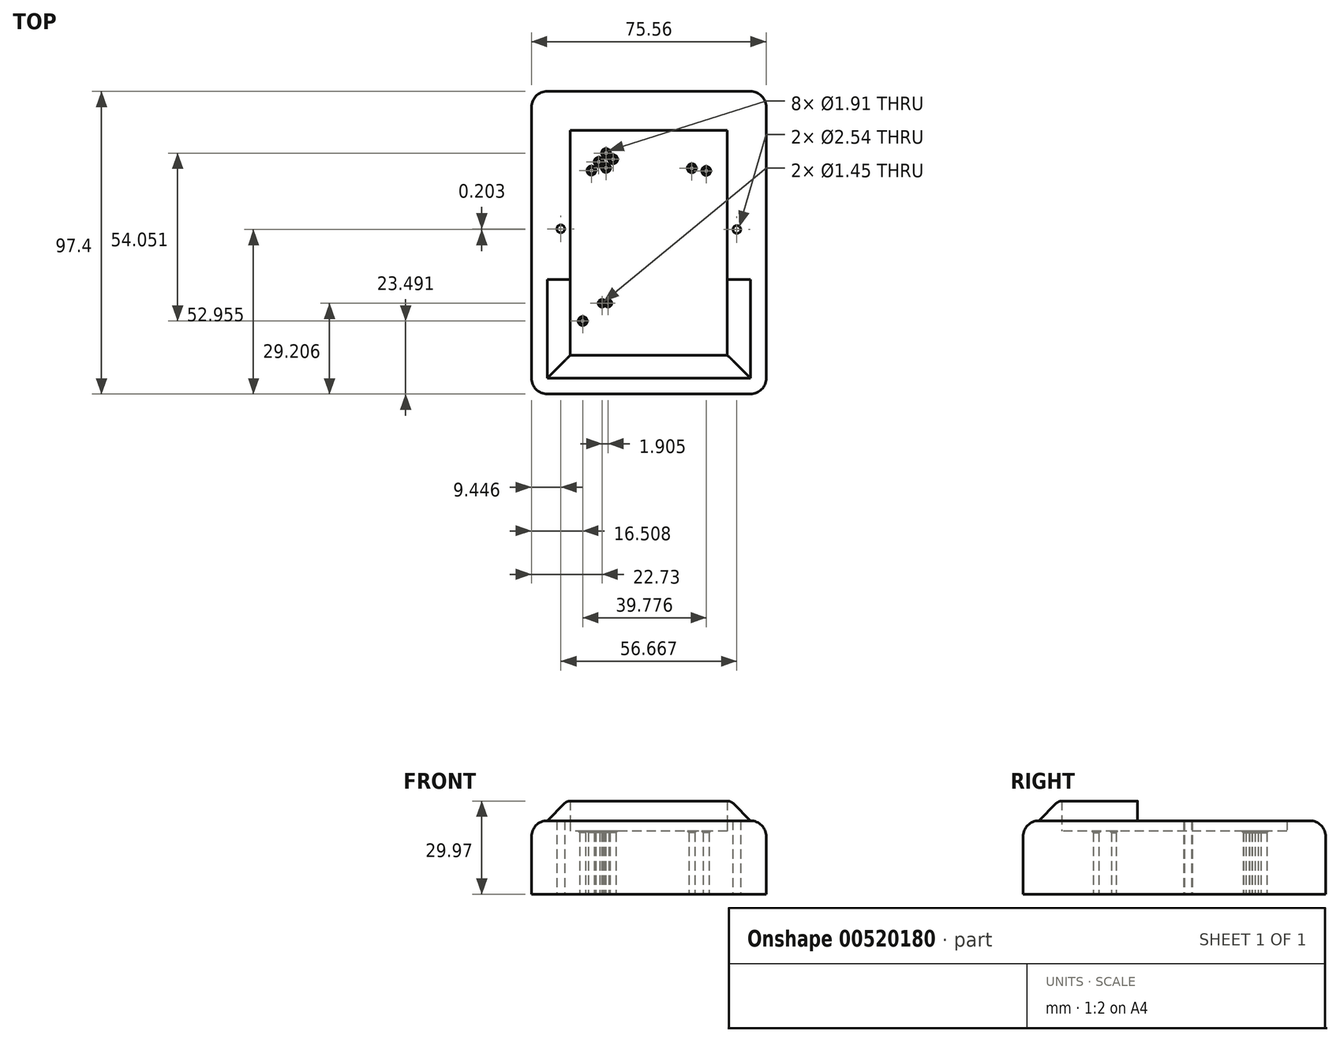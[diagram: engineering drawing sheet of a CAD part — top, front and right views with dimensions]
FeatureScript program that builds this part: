
annotation { "Feature Type Name" : "Feature", "Feature Type Description" : "" }
export const myFeature = defineFeature(function(context is Context, id is Id, definition is map)
    precondition{}
    {
        {
            var Q0;
            Q0=qCreatedBy(makeId("Top.planeOp"),FACE);
            var sketch = newSketch(context, id + "F0", { "sketchPlane" : qUnion([Q0])});
            skLineSegment(sketch, "E0.bottom", {"start": v(25.08, 36) * mm, "end": v(-25.08, 36) * mm});
            skLineSegment(sketch, "E0.top", {"start": v(25.08, -36) * mm, "end": v(-25.08, -36) * mm});
            skLineSegment(sketch, "E0.left", {"start": v(25.08, 36) * mm, "end": v(25.08, -36) * mm});
            skLineSegment(sketch, "E0.right", {"start": v(-25.08, 36) * mm, "end": v(-25.08, -36) * mm});
            skPoint(sketch, "E0.middle", {"position": v(0, 0) * mm});
            skCircle(sketch, "E1", {"center": v(-21.27, -25.2) * mm, "radius": 0.95 * mm});
            skCircle(sketch, "E2", {"center": v(-15.05, -19.5) * mm, "radius": 0.72 * mm});
            skCircle(sketch, "E3", {"center": v(-13.14, -19.5) * mm, "radius": 0.72 * mm});
            skCircle(sketch, "E4", {"center": v(-13.78, 24.07) * mm, "radius": 0.95 * mm});
            skCircle(sketch, "E5", {"center": v(-11.5, 26.86) * mm, "radius": 0.95 * mm});
            skCircle(sketch, "E6", {"center": v(-18.45, 23.2) * mm, "radius": 0.95 * mm});
            skCircle(sketch, "E7", {"center": v(-16.12, 26.02) * mm, "radius": 0.95 * mm});
            skCircle(sketch, "E8", {"center": v(-13.75, 28.84) * mm, "radius": 0.95 * mm});
            skCircle(sketch, "E9", {"center": v(13.86, 23.96) * mm, "radius": 0.95 * mm});
            skCircle(sketch, "E10", {"center": v(18.5, 23.1) * mm, "radius": 0.95 * mm});
            skLineSegment(sketch, "E11.bottom", {"start": v(25.29, 36.2) * mm, "end": v(-25.29, 36.2) * mm});
            skLineSegment(sketch, "E11.top", {"start": v(25.29, -36.2) * mm, "end": v(-25.29, -36.2) * mm});
            skLineSegment(sketch, "E11.left", {"start": v(25.29, 36.2) * mm, "end": v(25.29, -36.2) * mm});
            skLineSegment(sketch, "E11.right", {"start": v(-25.29, 36.2) * mm, "end": v(-25.29, -36.2) * mm});
            skLineSegment(sketch, "E12.bottom", {"start": v(-37.78, 48.7) * mm, "end": v(37.78, 48.7) * mm});
            skLineSegment(sketch, "E12.top", {"start": v(-37.78, -48.7) * mm, "end": v(37.78, -48.7) * mm});
            skLineSegment(sketch, "E12.left", {"start": v(-37.78, 48.7) * mm, "end": v(-37.78, -48.7) * mm});
            skLineSegment(sketch, "E12.right", {"start": v(37.78, 48.7) * mm, "end": v(37.78, -48.7) * mm});
            skCircle(sketch, "E13", {"center": v(-28.33, 4.46) * mm, "radius": 1.27 * mm});
            skCircle(sketch, "E14", {"center": v(28.33, 4.25) * mm, "radius": 1.27 * mm});
            skSolve(sketch);
        }
        {
            var Q0;
            Q0 = qSketchRegion(id + "F0", true);
            extrude(context, id + "F1", {"entities" : qUnion([Q0]), "depth" : 23.62 * mm, "offsetDistance" : 25.4 * mm});
        }
        {
            var Q0;
            Q0=makeQuery(id+"F0.imprint","IMPRINT",FACE,{"disambiguationData":[TD([[makeQuery(id+"F0.imprint","IMPRINT",EDGE,{"derivedFrom":sQuery(id+"F0.wireOp",EDGE,"E0.bottom")}),-1.0]])]});
            var Q1;
            Q1=makeQuery(id+"F0.imprint","IMPRINT",FACE,{"disambiguationData":[TD([[makeQuery(id+"F0.imprint","IMPRINT",EDGE,{"derivedFrom":sQuery(id+"F0.wireOp",EDGE,"E0.bottom")}),1.0]])]});
            extrude(context, id + "F2", {"entities" : qUnion([Q0, Q1]), "operationType" : NewBodyOperationType.ADD, "depth" : 20.32 * mm, "offsetDistance" : 25.4 * mm});
        }
        {
            var Q0;
            Q0=makeQuery(id+"F2.opExtrude","CAP_EDGE",EDGE,{"disambiguationData":[OSD([sQuery(id+"F0.wireOp",EDGE,"E8")])],"isStart":false});
            var Q1;
            Q1=makeQuery(id+"F2.opExtrude","CAP_EDGE",EDGE,{"disambiguationData":[OSD([sQuery(id+"F0.wireOp",EDGE,"E7")])],"isStart":false});
            var Q2;
            Q2=makeQuery(id+"F2.opExtrude","CAP_EDGE",EDGE,{"disambiguationData":[OSD([sQuery(id+"F0.wireOp",EDGE,"E6")])],"isStart":false});
            var Q3;
            Q3=makeQuery(id+"F2.opExtrude","CAP_EDGE",EDGE,{"disambiguationData":[OSD([sQuery(id+"F0.wireOp",EDGE,"E4")])],"isStart":false});
            var Q4;
            Q4=makeQuery(id+"F2.opExtrude","CAP_EDGE",EDGE,{"disambiguationData":[OSD([sQuery(id+"F0.wireOp",EDGE,"E5")])],"isStart":false});
            var Q5;
            Q5=makeQuery(id+"F2.opExtrude","CAP_EDGE",EDGE,{"disambiguationData":[OSD([sQuery(id+"F0.wireOp",EDGE,"E9")])],"isStart":false});
            var Q6;
            Q6=makeQuery(id+"F2.opExtrude","CAP_EDGE",EDGE,{"disambiguationData":[OSD([sQuery(id+"F0.wireOp",EDGE,"E10")])],"isStart":false});
            var Q7;
            Q7=makeQuery(id+"F2.opExtrude","CAP_EDGE",EDGE,{"disambiguationData":[OSD([sQuery(id+"F0.wireOp",EDGE,"E1")])],"isStart":false});
            var Q8;
            Q8=makeQuery(id+"F2.opExtrude","CAP_EDGE",EDGE,{"disambiguationData":[OSD([sQuery(id+"F0.wireOp",EDGE,"E2")])],"isStart":false});
            var Q9;
            Q9=makeQuery(id+"F2.opExtrude","CAP_EDGE",EDGE,{"disambiguationData":[OSD([sQuery(id+"F0.wireOp",EDGE,"E3")])],"isStart":false});
            chamfer(context, id + "F3", {"entities" : qUnion([Q0, Q1, Q2, Q3, Q4, Q5, Q6, Q7, Q8, Q9]), "width" : 0.5 * mm, "tangentPropagation" : true});
        }
        {
            var Q0;
            Q0=makeQuery(id+"F1.opExtrude","SWEPT_EDGE",EDGE,{"disambiguationData":[OSD([sQuery(id+"F0.wireOp",EDGE,"E12.bottom"),sQuery(id+"F0.wireOp",EDGE,"E12.left")])]});
            var Q1;
            Q1=makeQuery(id+"F1.opExtrude","SWEPT_EDGE",EDGE,{"disambiguationData":[OSD([sQuery(id+"F0.wireOp",EDGE,"E12.bottom"),sQuery(id+"F0.wireOp",EDGE,"E12.right")])]});
            var Q2;
            Q2=makeQuery(id+"F1.opExtrude","SWEPT_EDGE",EDGE,{"disambiguationData":[OSD([sQuery(id+"F0.wireOp",EDGE,"E12.top"),sQuery(id+"F0.wireOp",EDGE,"E12.right")])]});
            var Q3;
            Q3=makeQuery(id+"F1.opExtrude","SWEPT_EDGE",EDGE,{"disambiguationData":[OSD([sQuery(id+"F0.wireOp",EDGE,"E12.top"),sQuery(id+"F0.wireOp",EDGE,"E12.left")])]});
            var Q4;
            Q4=makeQuery(id+"F1.opExtrude","CAP_EDGE",EDGE,{"disambiguationData":[OSD([sQuery(id+"F0.wireOp",EDGE,"E12.right")])],"isStart":false});
            var Q5;
            Q5=makeQuery(id+"F1.opExtrude","CAP_EDGE",EDGE,{"disambiguationData":[OSD([sQuery(id+"F0.wireOp",EDGE,"E12.top")])],"isStart":false});
            var Q6;
            Q6=makeQuery(id+"F1.opExtrude","CAP_EDGE",EDGE,{"disambiguationData":[OSD([sQuery(id+"F0.wireOp",EDGE,"E12.left")])],"isStart":false});
            var Q7;
            Q7=makeQuery(id+"F1.opExtrude","CAP_EDGE",EDGE,{"disambiguationData":[OSD([sQuery(id+"F0.wireOp",EDGE,"E12.bottom")])],"isStart":false});
            fillet(context, id + "F4", {"entities" : qUnion([Q0, Q1, Q2, Q3, Q4, Q5, Q6, Q7]), "radius" : 5.08 * mm, "tangentPropagation" : true, "allowEdgeOverflow" : false});
        }
        {
            var Q0;
            Q0=makeQuery(id+"F1.opExtrude","CAP_FACE",FACE,{"disambiguationData":[OSD([sQuery(id+"F0.wireOp",EDGE,"E11.bottom"),sQuery(id+"F0.wireOp",EDGE,"E11.top"),sQuery(id+"F0.wireOp",EDGE,"E11.left"),sQuery(id+"F0.wireOp",EDGE,"E11.right"),sQuery(id+"F0.wireOp",EDGE,"E12.bottom"),sQuery(id+"F0.wireOp",EDGE,"E12.top"),sQuery(id+"F0.wireOp",EDGE,"E12.left"),sQuery(id+"F0.wireOp",EDGE,"E12.right"),sQuery(id+"F0.wireOp",EDGE,"E13"),sQuery(id+"F0.wireOp",EDGE,"E14")])],"isStart":false});
            var sketch = newSketch(context, id + "F5", { "sketchPlane" : qUnion([Q0])});
            skLineSegment(sketch, "E15.bottom", {"start": v(-25.29, -11.87) * mm, "end": v(-32.7, -11.87) * mm});
            skLineSegment(sketch, "E15.top", {"start": v(-25.29, -43.62) * mm, "end": v(-32.7, -43.62) * mm});
            skLineSegment(sketch, "E15.left", {"start": v(-25.29, -11.87) * mm, "end": v(-25.29, -43.62) * mm});
            skLineSegment(sketch, "E15.right", {"start": v(-32.7, -11.87) * mm, "end": v(-32.7, -43.62) * mm});
            skLineSegment(sketch, "E16.MirrorCS", {"start": v(25.29, -11.87) * mm, "end": v(32.7, -11.87) * mm});
            skLineSegment(sketch, "E17.MirrorCS", {"start": v(32.7, -11.87) * mm, "end": v(32.7, -43.62) * mm});
            skLineSegment(sketch, "E18.MirrorCS", {"start": v(25.29, -11.87) * mm, "end": v(25.29, -43.62) * mm});
            skLineSegment(sketch, "E19.MirrorCS", {"start": v(25.29, -43.62) * mm, "end": v(32.7, -43.62) * mm});
            skLineSegment(sketch, "E20.bottom", {"start": v(-25.29, -36.2) * mm, "end": v(25.29, -36.2) * mm});
            skLineSegment(sketch, "E20.top", {"start": v(-25.29, -43.62) * mm, "end": v(25.29, -43.62) * mm});
            skLineSegment(sketch, "E20.left", {"start": v(-25.29, -36.2) * mm, "end": v(-25.29, -43.62) * mm});
            skLineSegment(sketch, "E20.right", {"start": v(25.29, -36.2) * mm, "end": v(25.29, -43.62) * mm});
            skSolve(sketch);
        }
        {
            var Q0;
            Q0=makeQuery(id+"F5.imprint","IMPRINT",FACE,{"disambiguationData":[TD([[makeQuery(id+"F5.imprint","IMPRINT",EDGE,{"derivedFrom":sQuery(id+"F5.wireOp",EDGE,"E15.bottom")}),1.0]])]});
            var Q1;
            Q1=makeQuery(id+"F5.imprint","IMPRINT",FACE,{"disambiguationData":[TD([[makeQuery(id+"F5.imprint","IMPRINT",EDGE,{"derivedFrom":sQuery(id+"F5.wireOp",EDGE,"E20.bottom")}),1.0]])]});
            var Q2;
            Q2=makeQuery(id+"F5.imprint","IMPRINT",FACE,{"disambiguationData":[TD([[makeQuery(id+"F5.imprint","IMPRINT",EDGE,{"derivedFrom":sQuery(id+"F5.wireOp",EDGE,"E16.MirrorCS")}),-1.0]])]});
            extrude(context, id + "F6", {"entities" : qUnion([Q0, Q1, Q2]), "operationType" : NewBodyOperationType.ADD, "depth" : 6.35 * mm, "offsetDistance" : 25.4 * mm});
        }
        {
            var Q0;
            Q0=makeQuery(id+"F6.opExtrude","CAP_EDGE",EDGE,{"disambiguationData":[OSD([sQuery(id+"F5.wireOp",EDGE,"E15.top"),sQuery(id+"F5.wireOp",EDGE,"E19.MirrorCS"),sQuery(id+"F5.wireOp",EDGE,"E20.top")])],"isStart":false});
            var Q1;
            Q1=makeQuery(id+"F6.opExtrude","CAP_EDGE",EDGE,{"disambiguationData":[OSD([sQuery(id+"F5.wireOp",EDGE,"E15.right")])],"isStart":false});
            var Q2;
            Q2=makeQuery(id+"F6.opExtrude","CAP_EDGE",EDGE,{"disambiguationData":[OSD([sQuery(id+"F5.wireOp",EDGE,"E17.MirrorCS")])],"isStart":false});
            chamfer(context, id + "F7", {"entities" : qUnion([Q0, Q1, Q2]), "width" : 6.35 * mm, "tangentPropagation" : true});
        }
        {
            var Q0;
            {var subQ0=sQuery(id+"F5.wireOp",EDGE,"E20.top");var subQ1=sQuery(id+"F5.wireOp",EDGE,"E19.MirrorCS");var subQ2=sQuery(id+"F5.wireOp",EDGE,"E15.top");Q0=makeQuery(id+"F7.opChamfer","BLEND_EDGE",EDGE,{"blendedFrom":[makeQuery(id+"F6.opExtrude","CAP_EDGE",EDGE,{"disambiguationData":[OSD([subQ2,subQ1,subQ0])],"isStart":false}),makeQuery(id+"F6.opExtrude","CAP_FACE",FACE,{"disambiguationData":[OSD([sQuery(id+"F5.wireOp",EDGE,"E15.bottom"),subQ2,sQuery(id+"F5.wireOp",EDGE,"E15.left"),sQuery(id+"F5.wireOp",EDGE,"E15.right"),sQuery(id+"F5.wireOp",EDGE,"E16.MirrorCS"),sQuery(id+"F5.wireOp",EDGE,"E17.MirrorCS"),sQuery(id+"F5.wireOp",EDGE,"E18.MirrorCS"),subQ1,sQuery(id+"F5.wireOp",EDGE,"E20.bottom"),subQ0])],"isStart":false})],"blendedInto":[makeQuery(id+"F6.opExtrude","CAP_FACE",FACE,{"disambiguationData":[OSD([sQuery(id+"F5.wireOp",EDGE,"E15.bottom"),subQ2,sQuery(id+"F5.wireOp",EDGE,"E15.left"),sQuery(id+"F5.wireOp",EDGE,"E15.right"),sQuery(id+"F5.wireOp",EDGE,"E16.MirrorCS"),sQuery(id+"F5.wireOp",EDGE,"E17.MirrorCS"),sQuery(id+"F5.wireOp",EDGE,"E18.MirrorCS"),subQ1,sQuery(id+"F5.wireOp",EDGE,"E20.bottom"),subQ0])],"isStart":false})]});}
            var Q1;
            {var subQ0=sQuery(id+"F5.wireOp",EDGE,"E15.right");Q1=makeQuery(id+"F7.opChamfer","BLEND_EDGE",EDGE,{"blendedFrom":[makeQuery(id+"F6.opExtrude","CAP_EDGE",EDGE,{"disambiguationData":[OSD([subQ0])],"isStart":false}),makeQuery(id+"F6.opExtrude","CAP_FACE",FACE,{"disambiguationData":[OSD([sQuery(id+"F5.wireOp",EDGE,"E15.bottom"),sQuery(id+"F5.wireOp",EDGE,"E15.top"),sQuery(id+"F5.wireOp",EDGE,"E15.left"),subQ0,sQuery(id+"F5.wireOp",EDGE,"E16.MirrorCS"),sQuery(id+"F5.wireOp",EDGE,"E17.MirrorCS"),sQuery(id+"F5.wireOp",EDGE,"E18.MirrorCS"),sQuery(id+"F5.wireOp",EDGE,"E19.MirrorCS"),sQuery(id+"F5.wireOp",EDGE,"E20.bottom"),sQuery(id+"F5.wireOp",EDGE,"E20.top")])],"isStart":false})],"blendedInto":[makeQuery(id+"F6.opExtrude","CAP_FACE",FACE,{"disambiguationData":[OSD([sQuery(id+"F5.wireOp",EDGE,"E15.bottom"),sQuery(id+"F5.wireOp",EDGE,"E15.top"),sQuery(id+"F5.wireOp",EDGE,"E15.left"),subQ0,sQuery(id+"F5.wireOp",EDGE,"E16.MirrorCS"),sQuery(id+"F5.wireOp",EDGE,"E17.MirrorCS"),sQuery(id+"F5.wireOp",EDGE,"E18.MirrorCS"),sQuery(id+"F5.wireOp",EDGE,"E19.MirrorCS"),sQuery(id+"F5.wireOp",EDGE,"E20.bottom"),sQuery(id+"F5.wireOp",EDGE,"E20.top")])],"isStart":false})]});}
            var Q2;
            {var subQ0=sQuery(id+"F5.wireOp",EDGE,"E17.MirrorCS");Q2=makeQuery(id+"F7.opChamfer","BLEND_EDGE",EDGE,{"blendedFrom":[makeQuery(id+"F6.opExtrude","CAP_EDGE",EDGE,{"disambiguationData":[OSD([subQ0])],"isStart":false}),makeQuery(id+"F6.opExtrude","CAP_FACE",FACE,{"disambiguationData":[OSD([sQuery(id+"F5.wireOp",EDGE,"E15.bottom"),sQuery(id+"F5.wireOp",EDGE,"E15.top"),sQuery(id+"F5.wireOp",EDGE,"E15.left"),sQuery(id+"F5.wireOp",EDGE,"E15.right"),sQuery(id+"F5.wireOp",EDGE,"E16.MirrorCS"),subQ0,sQuery(id+"F5.wireOp",EDGE,"E18.MirrorCS"),sQuery(id+"F5.wireOp",EDGE,"E19.MirrorCS"),sQuery(id+"F5.wireOp",EDGE,"E20.bottom"),sQuery(id+"F5.wireOp",EDGE,"E20.top")])],"isStart":false})],"blendedInto":[makeQuery(id+"F6.opExtrude","CAP_FACE",FACE,{"disambiguationData":[OSD([sQuery(id+"F5.wireOp",EDGE,"E15.bottom"),sQuery(id+"F5.wireOp",EDGE,"E15.top"),sQuery(id+"F5.wireOp",EDGE,"E15.left"),sQuery(id+"F5.wireOp",EDGE,"E15.right"),sQuery(id+"F5.wireOp",EDGE,"E16.MirrorCS"),subQ0,sQuery(id+"F5.wireOp",EDGE,"E18.MirrorCS"),sQuery(id+"F5.wireOp",EDGE,"E19.MirrorCS"),sQuery(id+"F5.wireOp",EDGE,"E20.bottom"),sQuery(id+"F5.wireOp",EDGE,"E20.top")])],"isStart":false})]});}
            var Q3;
            Q3=makeQuery(id+"F6.opExtrude","CAP_EDGE",EDGE,{"disambiguationData":[OSD([sQuery(id+"F5.wireOp",EDGE,"E15.bottom")])],"isStart":true});
            var Q4;
            Q4=makeQuery(id+"F6.opExtrude","CAP_EDGE",EDGE,{"disambiguationData":[OSD([sQuery(id+"F5.wireOp",EDGE,"E16.MirrorCS")])],"isStart":true});
            fillet(context, id + "F8", {"entities" : qUnion([Q0, Q1, Q2, Q3, Q4]), "radius" : 2.54 * mm, "tangentPropagation" : true, "allowEdgeOverflow" : false});
        }
    });
